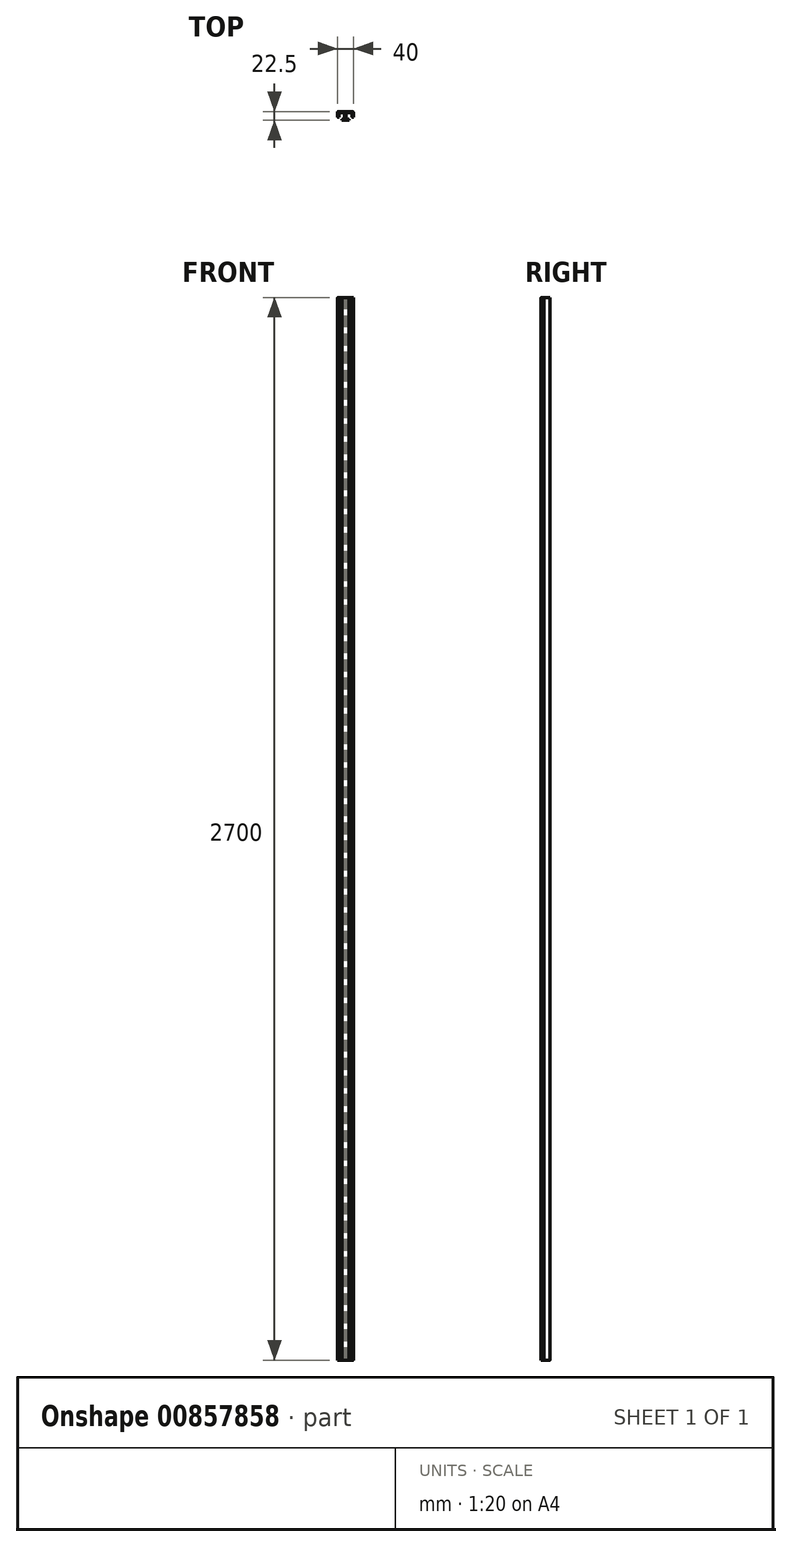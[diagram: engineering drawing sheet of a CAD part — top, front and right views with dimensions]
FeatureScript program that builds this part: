
annotation { "Feature Type Name" : "Feature", "Feature Type Description" : "" }
export const myFeature = defineFeature(function(context is Context, id is Id, definition is map)
    precondition{}
    {
        {
            var Q0;
            Q0=qCreatedBy(makeId("Top.planeOp"),FACE);
            var sketch = newSketch(context, id + "F0", { "sketchPlane" : qUnion([Q0])});
            skLineSegment(sketch, "E0", {"start": v(-20, 10) * mm, "end": v(20, 10) * mm});
            skLineSegment(sketch, "E1", {"start": v(20, 10) * mm, "end": v(20, -5) * mm});
            skLineSegment(sketch, "E2", {"start": v(-20, 10) * mm, "end": v(-20, -5) * mm});
            skLineSegment(sketch, "E3.0", {"start": v(-17, 7) * mm, "end": v(-17, -5) * mm});
            skLineSegment(sketch, "E3.1", {"start": v(-17, 7) * mm, "end": v(-2, 7) * mm});
            skLineSegment(sketch, "E3.2", {"start": v(17, 7) * mm, "end": v(17, -5) * mm});
            skLineSegment(sketch, "E4", {"start": v(-20, -5) * mm, "end": v(-17, -5) * mm});
            skLineSegment(sketch, "E5", {"start": v(17, -5) * mm, "end": v(20, -5) * mm});
            skLineSegment(sketch, "E6", {"start": v(-2, 7) * mm, "end": v(-2, -9.5) * mm});
            skLineSegment(sketch, "E7", {"start": v(-2, -9.5) * mm, "end": v(-8.5, -9.5) * mm});
            skLineSegment(sketch, "E8", {"start": v(-8.5, -9.5) * mm, "end": v(-8.5, -12.5) * mm});
            skLineSegment(sketch, "E9", {"start": v(-8.5, -12.5) * mm, "end": v(0, -12.5) * mm});
            skLineSegment(sketch, "E10.MirrorCS", {"start": v(8.5, -12.5) * mm, "end": v(0, -12.5) * mm});
            skLineSegment(sketch, "E11.MirrorCS", {"start": v(8.5, -9.5) * mm, "end": v(8.5, -12.5) * mm});
            skLineSegment(sketch, "E12.MirrorCS", {"start": v(2, 7) * mm, "end": v(2, -9.5) * mm});
            skLineSegment(sketch, "E13.MirrorCS", {"start": v(2, -9.5) * mm, "end": v(8.5, -9.5) * mm});
            skLineSegment(sketch, "E14.trimOffspring", {"start": v(2, 7) * mm, "end": v(17, 7) * mm});
            skSolve(sketch);
        }
        {
            var Q0;
            Q0=qSketchRegion(id+"F0",true);
            extrude(context, id + "F1", {"entities" : qUnion([Q0]), "depth" : 2700 * mm, "offsetDistance" : 25 * mm});
        }
        {
            var Q0;
            Q0=makeQuery(id+"F1.opExtrude","SWEPT_EDGE",EDGE,{"disambiguationData":[OSD([sQuery(id+"F0.wireOp",EDGE,"E0"),sQuery(id+"F0.wireOp",EDGE,"E2")])]});
            var Q1;
            Q1=makeQuery(id+"F1.opExtrude","SWEPT_EDGE",EDGE,{"disambiguationData":[OSD([sQuery(id+"F0.wireOp",EDGE,"E0"),sQuery(id+"F0.wireOp",EDGE,"E1")])]});
            fillet(context, id + "F2", {"entities" : qUnion([Q0, Q1]), "radius" : 2 * mm, "tangentPropagation" : true, "allowEdgeOverflow" : false});
        }
        {
            var Q0;
            Q0=makeQuery(id+"F1.opExtrude","SWEPT_EDGE",EDGE,{"disambiguationData":[OSD([sQuery(id+"F0.wireOp",EDGE,"E3.0"),sQuery(id+"F0.wireOp",EDGE,"E3.1")])]});
            var Q1;
            Q1=makeQuery(id+"F1.opExtrude","SWEPT_EDGE",EDGE,{"disambiguationData":[OSD([sQuery(id+"F0.wireOp",EDGE,"E3.0"),sQuery(id+"F0.wireOp",EDGE,"E4")])]});
            var Q2;
            Q2=makeQuery(id+"F1.opExtrude","SWEPT_EDGE",EDGE,{"disambiguationData":[OSD([sQuery(id+"F0.wireOp",EDGE,"E2"),sQuery(id+"F0.wireOp",EDGE,"E4")])]});
            var Q3;
            Q3=makeQuery(id+"F1.opExtrude","SWEPT_EDGE",EDGE,{"disambiguationData":[OSD([sQuery(id+"F0.wireOp",EDGE,"E8"),sQuery(id+"F0.wireOp",EDGE,"E9")])]});
            var Q4;
            Q4=makeQuery(id+"F1.opExtrude","SWEPT_EDGE",EDGE,{"disambiguationData":[OSD([sQuery(id+"F0.wireOp",EDGE,"E10.MirrorCS"),sQuery(id+"F0.wireOp",EDGE,"E11.MirrorCS")])]});
            var Q5;
            Q5=makeQuery(id+"F1.opExtrude","SWEPT_EDGE",EDGE,{"disambiguationData":[OSD([sQuery(id+"F0.wireOp",EDGE,"E11.MirrorCS"),sQuery(id+"F0.wireOp",EDGE,"E13.MirrorCS")])]});
            var Q6;
            Q6=makeQuery(id+"F1.opExtrude","SWEPT_EDGE",EDGE,{"disambiguationData":[OSD([sQuery(id+"F0.wireOp",EDGE,"E3.2"),sQuery(id+"F0.wireOp",EDGE,"E5")])]});
            var Q7;
            Q7=makeQuery(id+"F1.opExtrude","SWEPT_EDGE",EDGE,{"disambiguationData":[OSD([sQuery(id+"F0.wireOp",EDGE,"E1"),sQuery(id+"F0.wireOp",EDGE,"E5")])]});
            var Q8;
            Q8=makeQuery(id+"F1.opExtrude","SWEPT_EDGE",EDGE,{"disambiguationData":[OSD([sQuery(id+"F0.wireOp",EDGE,"E12.MirrorCS"),sQuery(id+"F0.wireOp",EDGE,"E14.trimOffspring")])]});
            var Q9;
            Q9=makeQuery(id+"F1.opExtrude","SWEPT_EDGE",EDGE,{"disambiguationData":[OSD([sQuery(id+"F0.wireOp",EDGE,"E3.2"),sQuery(id+"F0.wireOp",EDGE,"E14.trimOffspring")])]});
            var Q10;
            Q10=makeQuery(id+"F1.opExtrude","SWEPT_EDGE",EDGE,{"disambiguationData":[OSD([sQuery(id+"F0.wireOp",EDGE,"E3.1"),sQuery(id+"F0.wireOp",EDGE,"E6")])]});
            var Q11;
            Q11=makeQuery(id+"F1.opExtrude","SWEPT_EDGE",EDGE,{"disambiguationData":[OSD([sQuery(id+"F0.wireOp",EDGE,"E7"),sQuery(id+"F0.wireOp",EDGE,"E8")])]});
            var Q12;
            Q12=makeQuery(id+"F1.opExtrude","SWEPT_EDGE",EDGE,{"disambiguationData":[OSD([sQuery(id+"F0.wireOp",EDGE,"E6"),sQuery(id+"F0.wireOp",EDGE,"E7")])]});
            var Q13;
            Q13=makeQuery(id+"F1.opExtrude","SWEPT_EDGE",EDGE,{"disambiguationData":[OSD([sQuery(id+"F0.wireOp",EDGE,"E12.MirrorCS"),sQuery(id+"F0.wireOp",EDGE,"E13.MirrorCS")])]});
            fillet(context, id + "F3", {"entities" : qUnion([Q0, Q1, Q2, Q3, Q4, Q5, Q6, Q7, Q8, Q9, Q10, Q11, Q12, Q13]), "radius" : 1 * mm, "tangentPropagation" : true, "allowEdgeOverflow" : false});
        }
    });
